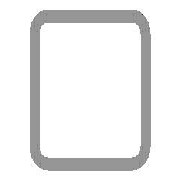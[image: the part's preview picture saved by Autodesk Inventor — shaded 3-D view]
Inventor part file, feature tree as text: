
AUTODESK INVENTOR PART (.ipt)
format: ipt  version: 2022 (Build 260153000, 153)  size: 563,200 bytes
history: native  units: mm (DEFAULTED — no unit token found)
features: other x5, sketch x5, hole x2, extrude x1, plane x1
ambient origin geometry x8: Origin, YZ Plane, XZ Plane, XY Plane, X Axis, Y Axis, Z Axis, Center Point
bodies: Solid1 (feature_tree), Solid3 (feature_tree)
feature tree (14):
  parser-record x1  (decoder bookkeeping rows leaked as tree rows — omitted from the tree; the rows remain in map.json)
  other  "Driven Length"
  other  "Plano inicial"
  other  "Plano final"
  extrude  "Cuerpo"  TaperAngle=0.0deg  [1 undecoded]
  hole  "Hole3"  [1 undecoded]
  hole  "Hole4"  [1 undecoded]
  sketch  "Boceto"  dims[d14=470.0mm d15=20.0mm d16=20.0mm d17=90.0deg d18=460.0mm d33=11.0mm d34=6.0mm d35=4.0mm d36=2.0mm d37=90.0deg d38=8.0mm d39=0.0mm d40=11.0mm d41=6.0mm d42=4.0mm d43=2.0mm d44=90.0deg d45=8.0mm d46=0.0mm]
  sketch  "Sketch3"  dims[d3=460.0mm d4=0.0mm]
  plane  "Work Plane3"
  sketch  "Sketch4"  dims[d7=7.5mm d10=40.0mm]
  sketch  "Sketch7"  dims[d11=40.0mm d12=5.0mm]
  sketch  "Sketch8"  dims[d13=10.0mm]
  other  "Srf2"
note: 3 required parameter values undecoded (feature->parameter linkage not recoverable at this tier; creation-order binding heuristic only, values carry confidence <= 0.55)
